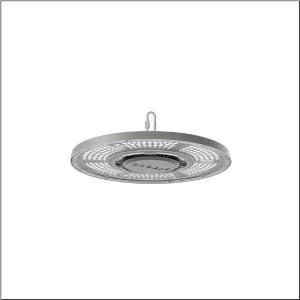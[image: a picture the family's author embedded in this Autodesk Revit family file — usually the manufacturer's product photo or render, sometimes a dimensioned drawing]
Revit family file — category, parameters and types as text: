
# Revit family: highbay_31-s_51hc417a4fmb
name_source: partatom
category: Lighting Fixtures
units: mm (PartAtom-declared; Revit-internal decimal feet)

## family parameters
Cut with Voids When Loaded = No
Host = Face
Light Source = No
Part Type = Normal
Room Calculation Point = No
Round Connector Dimension = Use Diameter
Shared = No

## types (1)
- Highbay 31-S (1 x LED, 14000 lm, 94 W, 4000K)
    Apparent Load = 94 VA
    CIE Flux Codes = 94 98 100 100 100
    Color Rendering = 80
    Color Temperature = 4000K
    Default Elevation = 1800 mm
    Description = Highbay 31-S, LED high bay luminaire, primary light control with lens, of PC, primary optical cover: cover panel, of PC, transparent, light emission: direct distribution, primary light characteristic: rotationally symmetric, installation type: suspended mounting, surface-mounted, LED, rated luminous flux: 14.000lm, luminous efficacy: 150lm/W, light colour: 840, colour temperature: 4000K, control gear: ECG, with cable, 3x 1.0mm², free wire ends, mains connection: 220..240V, AC/DC, 0/50..60Hz, cable length: 1,5m, rated input power: 94W, housing, rotationally symmetric, of diecast aluminium, powder-coated, grey aluminium (RAL 9007), with hook on luminaire side, incl. screw, diameter: 339mm, protection rating (complete): IP65, insulation class (complete): insulation class I (protective earthing), certification: CE, ENEC, UKCA, protection symbol: D, impact resistance: IK08, permissible operating ambient temperature: -30..+45°C, standard: EN 60598-2-22, EN 60598, corresponds to IFS (International Featured Standards) requirements for safety and quality in the food industry, packaging unit: 1 piece
    Height = 141 mm
    Lamp = 1 x LED
    Lamp Light Flux = 14000 lm
    Lamp Power = 94 W
    Lamp count = 1
    Length = 339 mm
    Luminous efficacy = 149 lm/W
    Manufacturer = Siteco
    ModVariant = No
    Model = 51HC417A4FMB
    Mounting Place = Ceiling
    Mounting Type = Pendant
    Number of Poles = 1
    OnlyDefault = Yes
    Power Factor = 1
    Product Name = Highbay 31-S
    Product group = LED high bay luminaire
    ProductGroupID = 903
    Protection Class = Protection class I
    Protection Degree = IP 65
    RLX_Detail_Level = 1
    RLX_Emergency_Light_Flux = 0 lm
    RLX_Emergency_Type = 0
    RLX_Emergency_Type_DB = No
    RlxData = <blob elided: 107677 chars, md5=2b31eee3>
    Socket = socket
    Standby Power = 0 W
    System Light Flux = 14000 lm
    System Power = 94 W
    Type Comments = Product without accessories
    Type Image = l_1007237.jpg
    URL = http://relux.com
    VarID = ---
    Voltage = 0 V
    Weight = 0.00 kg
    Width = 0 mm  [stored 0 ft]

note: [stored X ft] marks values corroborated as IEEE doubles in the binary element streams (Revit-internal decimal feet)

## geometry (parser evidence)
native form markers: Blend x4, Sweep x9
no freeform markers — native parametric forms only
